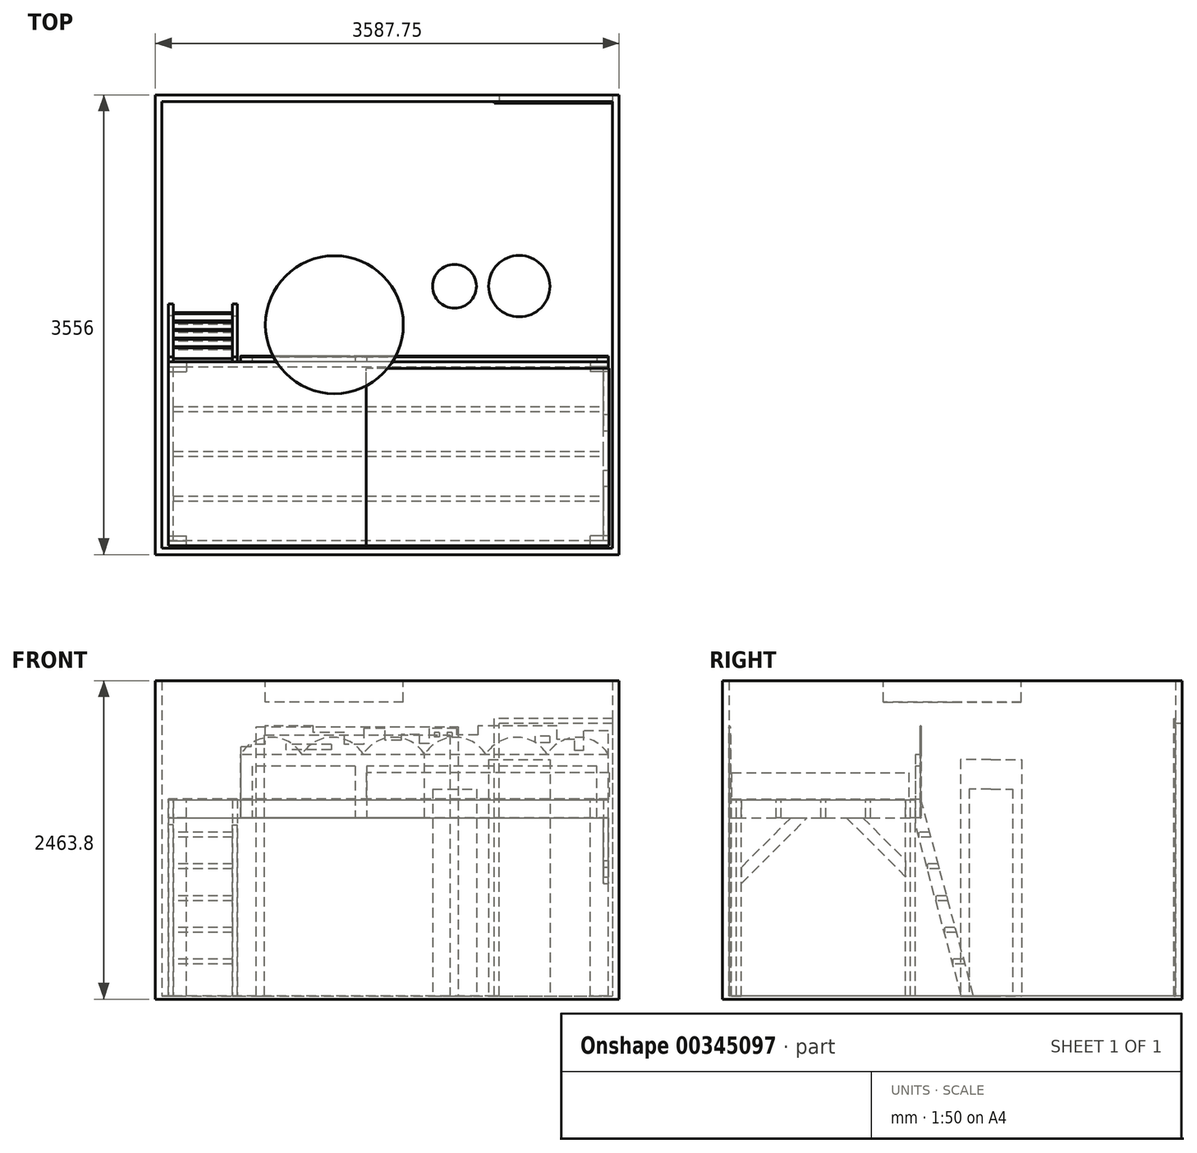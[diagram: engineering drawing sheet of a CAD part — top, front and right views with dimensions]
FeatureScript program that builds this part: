
annotation { "Feature Type Name" : "Feature", "Feature Type Description" : "" }
export const myFeature = defineFeature(function(context is Context, id is Id, definition is map)
    precondition{}
    {
        {
            var Q0;
            Q0=qCreatedBy(makeId("Top.planeOp"),FACE);
            var sketch = newSketch(context, id + "F0", { "sketchPlane" : qUnion([Q0])});
            skLineSegment(sketch, "E0.bottom", {"start": v(-2262.88, 2923.08) * mm, "end": v(-56.88, 2923.08) * mm});
            skLineSegment(sketch, "E0.top", {"start": v(-2262.88, -531.32) * mm, "end": v(1223.27, -531.32) * mm});
            skLineSegment(sketch, "E0.left", {"start": v(-2262.88, 2923.08) * mm, "end": v(-2262.88, -531.32) * mm});
            skLineSegment(sketch, "E0.right", {"start": v(1223.27, 2923.08) * mm, "end": v(1223.27, -531.32) * mm});
            skLineSegment(sketch, "E1.0", {"start": v(-2313.68, 2973.88) * mm, "end": v(-56.88, 2973.88) * mm});
            skLineSegment(sketch, "E1.1", {"start": v(-2313.68, 2973.88) * mm, "end": v(-2313.68, -582.12) * mm});
            skLineSegment(sketch, "E1.2", {"start": v(-2313.68, -582.12) * mm, "end": v(1274.07, -582.12) * mm});
            skLineSegment(sketch, "E1.3", {"start": v(1274.07, 2973.88) * mm, "end": v(1274.07, -582.12) * mm});
            skLineSegment(sketch, "E2.bottom", {"start": v(-94.98, 2923.08) * mm, "end": v(-56.88, 2923.08) * mm});
            skLineSegment(sketch, "E2.top", {"start": v(-94.98, 2910.38) * mm, "end": v(-56.88, 2910.38) * mm});
            skLineSegment(sketch, "E2.left", {"start": v(-94.98, 2923.08) * mm, "end": v(-94.98, 2910.38) * mm});
            skLineSegment(sketch, "E2.right", {"start": v(-56.88, 2923.08) * mm, "end": v(-56.88, 2910.38) * mm});
            skLineSegment(sketch, "E3", {"start": v(-56.88, 2923.08) * mm, "end": v(-56.88, 2973.88) * mm});
            skLineSegment(sketch, "E4", {"start": v(1274.07, 2973.88) * mm, "end": v(1223.27, 2973.88) * mm});
            skLineSegment(sketch, "E5", {"start": v(1223.27, 2973.88) * mm, "end": v(1223.27, 2923.08) * mm});
            skLineSegment(sketch, "E6", {"start": v(-56.88, 2973.88) * mm, "end": v(1223.27, 2973.88) * mm});
            skLineSegment(sketch, "E7", {"start": v(1223.27, 2923.08) * mm, "end": v(-56.88, 2923.08) * mm});
            skSolve(sketch);
        }
        {
            var Q0;
            Q0=qSketchRegion(id+"F0",true);
            extrude(context, id + "F1", {"entities" : qUnion([Q0]), "depth" : 2438.4 * mm});
        }
        {
            var Q0;
            Q0=makeQuery(id+"F1.opExtrude","SWEPT_FACE",FACE,{"disambiguationData":[OSD([sQuery(id+"F0.wireOp",EDGE,"E0.bottom"),sQuery(id+"F0.wireOp",EDGE,"E2.bottom"),sQuery(id+"F0.wireOp",EDGE,"E7")])]});
            var sketch = newSketch(context, id + "F2", { "sketchPlane" : qUnion([Q0])});
            skLineSegment(sketch, "E8.bottom", {"start": v(1223.27, 0) * mm, "end": v(346.97, 0) * mm});
            skLineSegment(sketch, "E8.top", {"start": v(1223.27, 2108.2) * mm, "end": v(346.97, 2108.2) * mm});
            skLineSegment(sketch, "E8.left", {"start": v(1223.27, 0) * mm, "end": v(1223.27, 2108.2) * mm});
            skLineSegment(sketch, "E8.right", {"start": v(346.97, 0) * mm, "end": v(346.97, 2108.2) * mm});
            skSolve(sketch);
        }
        {
            var Q0;
            Q0=qSketchRegion(id+"F2",true);
            extrude(context, id + "F3", {"entities" : qUnion([Q0]), "operationType" : NewBodyOperationType.REMOVE, "endBound" : BoundingType.UP_TO_NEXT, "oppositeDirection" : true, "depth" : 25.4 * mm});
        }
        {
            var Q0;
            Q0=makeQuery(id+"F1.opExtrude","SWEPT_FACE",FACE,{"disambiguationData":[OSD([sQuery(id+"F0.wireOp",EDGE,"E0.bottom"),sQuery(id+"F0.wireOp",EDGE,"E2.bottom"),sQuery(id+"F0.wireOp",EDGE,"E7")])]});
            var sketch = newSketch(context, id + "F4", { "sketchPlane" : qUnion([Q0])});
            skLineSegment(sketch, "E9.bottom", {"start": v(346.97, 0) * mm, "end": v(308.87, 0) * mm});
            skLineSegment(sketch, "E9.top", {"start": v(346.97, 2146.3) * mm, "end": v(308.87, 2146.3) * mm});
            skLineSegment(sketch, "E9.left", {"start": v(346.97, 0) * mm, "end": v(346.97, 2146.3) * mm});
            skLineSegment(sketch, "E9.right", {"start": v(308.87, 0) * mm, "end": v(308.87, 2146.3) * mm});
            skLineSegment(sketch, "E10.bottom", {"start": v(346.97, 2146.3) * mm, "end": v(1223.27, 2146.3) * mm});
            skLineSegment(sketch, "E10.top", {"start": v(346.97, 2108.2) * mm, "end": v(1223.27, 2108.2) * mm});
            skLineSegment(sketch, "E10.left", {"start": v(346.97, 2146.3) * mm, "end": v(346.97, 2108.2) * mm});
            skLineSegment(sketch, "E10.right", {"start": v(1223.27, 2146.3) * mm, "end": v(1223.27, 2108.2) * mm});
            skSolve(sketch);
        }
        {
            var Q0;
            Q0=qSketchRegion(id+"F4",true);
            extrude(context, id + "F5", {"entities" : qUnion([Q0]), "operationType" : NewBodyOperationType.ADD, "depth" : 12.7 * mm});
        }
        {
            var Q0;
            Q0=makeQuery(id+"F1.opExtrude","CAP_FACE",FACE,{"disambiguationData":[OSD([sQuery(id+"F0.wireOp",EDGE,"E0.bottom"),sQuery(id+"F0.wireOp",EDGE,"E0.top"),sQuery(id+"F0.wireOp",EDGE,"E0.left"),sQuery(id+"F0.wireOp",EDGE,"E0.right"),sQuery(id+"F0.wireOp",EDGE,"E1.0"),sQuery(id+"F0.wireOp",EDGE,"E1.1"),sQuery(id+"F0.wireOp",EDGE,"E1.2"),sQuery(id+"F0.wireOp",EDGE,"E1.3"),sQuery(id+"F0.wireOp",EDGE,"E2.bottom"),sQuery(id+"F0.wireOp",EDGE,"E4"),sQuery(id+"F0.wireOp",EDGE,"E6"),sQuery(id+"F0.wireOp",EDGE,"E7")])],"isStart":false});
            var sketch = newSketch(context, id + "F6", { "sketchPlane" : qUnion([Q0])});
            skCircle(sketch, "E11", {"center": v(-929.38, 1195.88) * mm, "radius": 533.4 * mm});
            skSolve(sketch);
        }
        {
            var Q0;
            Q0=qSketchRegion(id+"F6",true);
            extrude(context, id + "F7", {"entities" : qUnion([Q0]), "oppositeDirection" : true, "depth" : 165.1 * mm});
        }
        {
            var Q0;
            Q0=makeQuery(id+"F5.boolean.opBoolean","MERGE",FACE,{"derivedFrom":[makeQuery(id+"F1.opExtrude","CAP_FACE",FACE,{"disambiguationData":[OSD([sQuery(id+"F0.wireOp",EDGE,"E0.bottom"),sQuery(id+"F0.wireOp",EDGE,"E0.top"),sQuery(id+"F0.wireOp",EDGE,"E0.left"),sQuery(id+"F0.wireOp",EDGE,"E0.right"),sQuery(id+"F0.wireOp",EDGE,"E1.0"),sQuery(id+"F0.wireOp",EDGE,"E1.1"),sQuery(id+"F0.wireOp",EDGE,"E1.2"),sQuery(id+"F0.wireOp",EDGE,"E1.3"),sQuery(id+"F0.wireOp",EDGE,"E2.bottom"),sQuery(id+"F0.wireOp",EDGE,"E4"),sQuery(id+"F0.wireOp",EDGE,"E6"),sQuery(id+"F0.wireOp",EDGE,"E7")])],"isStart":true}),makeQuery(id+"F5.opExtrude","SWEPT_FACE",FACE,{"disambiguationData":[OSD([sQuery(id+"F4.wireOp",EDGE,"E9.bottom")])]})]});
            var sketch = newSketch(context, id + "F8", { "sketchPlane" : qUnion([Q0])});
            skLineSegment(sketch, "E12.bottom", {"start": v(-2313.68, -2973.88) * mm, "end": v(1274.07, -2973.88) * mm});
            skLineSegment(sketch, "E12.top", {"start": v(-2313.68, 582.12) * mm, "end": v(1274.07, 582.12) * mm});
            skLineSegment(sketch, "E12.left", {"start": v(-2313.68, -2973.88) * mm, "end": v(-2313.68, 582.12) * mm});
            skLineSegment(sketch, "E12.right", {"start": v(1274.07, -2973.88) * mm, "end": v(1274.07, 582.12) * mm});
            skSolve(sketch);
        }
        {
            var Q0;
            Q0=qSketchRegion(id+"F8",true);
            extrude(context, id + "F9", {"entities" : qUnion([Q0]), "operationType" : NewBodyOperationType.ADD, "depth" : 25.4 * mm});
        }
        {
            var Q0;
            Q0=makeQuery(id+"F9.opExtrude","CAP_FACE",FACE,{"disambiguationData":[OSD([sQuery(id+"F8.wireOp",EDGE,"E12.bottom"),sQuery(id+"F8.wireOp",EDGE,"E12.top"),sQuery(id+"F8.wireOp",EDGE,"E12.left"),sQuery(id+"F8.wireOp",EDGE,"E12.right")])],"isStart":true});
            cPlane(context, id + "F10", {"entities" : qUnion([Q0]), "cplaneType" : CPlaneType.OFFSET, "offset" : 1524 * mm, "width" : 152.4 * mm, "height" : 152.4 * mm});
        }
        {
            var Q0;
            Q0=makeQuery(id+"F1.opExtrude","SWEPT_FACE",FACE,{"disambiguationData":[OSD([sQuery(id+"F0.wireOp",EDGE,"E0.top")])]});
            var sketch = newSketch(context, id + "F11", { "sketchPlane" : qUnion([Q0])});
            skLineSegment(sketch, "E13.bottom", {"start": v(1532.63, 0) * mm, "end": v(1469.13, 0) * mm});
            skLineSegment(sketch, "E13.top", {"start": v(1532.63, 2082.8) * mm, "end": v(1469.13, 2082.8) * mm});
            skLineSegment(sketch, "E13.left", {"start": v(1532.63, 0) * mm, "end": v(1532.63, 2082.8) * mm});
            skLineSegment(sketch, "E13.right", {"start": v(1469.13, 0) * mm, "end": v(1469.13, 2082.8) * mm});
            skLineSegment(sketch, "E14.bottom", {"start": v(1469.13, 2082.8) * mm, "end": v(34.03, 2082.8) * mm});
            skLineSegment(sketch, "E14.top", {"start": v(1469.13, 2019.3) * mm, "end": v(34.03, 2019.3) * mm});
            skLineSegment(sketch, "E14.left", {"start": v(1469.13, 2082.8) * mm, "end": v(1469.13, 2019.3) * mm});
            skLineSegment(sketch, "E14.right", {"start": v(34.03, 2082.8) * mm, "end": v(34.03, 2019.3) * mm});
            skLineSegment(sketch, "E15.bottom", {"start": v(34.03, 2082.8) * mm, "end": v(-29.47, 2082.8) * mm});
            skLineSegment(sketch, "E15.top", {"start": v(34.03, 0) * mm, "end": v(-29.47, 0) * mm});
            skLineSegment(sketch, "E15.left", {"start": v(34.03, 2082.8) * mm, "end": v(34.03, 0) * mm});
            skLineSegment(sketch, "E15.right", {"start": v(-29.47, 2082.8) * mm, "end": v(-29.47, 0) * mm});
            skSolve(sketch);
        }
        {
            var Q0;
            Q0=qSketchRegion(id+"F11",true);
            extrude(context, id + "F12", {"entities" : qUnion([Q0]), "operationType" : NewBodyOperationType.ADD, "depth" : 12.7 * mm});
        }
        {
            var Q0;
            Q0=qCreatedBy(id+"F10.planeOp",FACE);
            var sketch = newSketch(context, id + "F13", { "sketchPlane" : qUnion([Q0])});
            skLineSegment(sketch, "E16.bottom", {"start": v(1197.87, -512.27) * mm, "end": v(-681.73, -512.27) * mm});
            skLineSegment(sketch, "E16.top", {"start": v(1197.87, 859.33) * mm, "end": v(-681.73, 859.33) * mm});
            skLineSegment(sketch, "E16.left", {"start": v(1197.87, -512.27) * mm, "end": v(1197.87, 859.33) * mm});
            skLineSegment(sketch, "E16.right", {"start": v(-681.73, -512.27) * mm, "end": v(-681.73, 859.33) * mm});
            skSolve(sketch);
        }
        {
            var Q0;
            Q0=qSketchRegion(id+"F13",true);
            extrude(context, id + "F14", {"entities" : qUnion([Q0]), "depth" : 203.2 * mm});
        }
        {
            var Q0;
            Q0=qCreatedBy(id+"F10.planeOp",FACE);
            var sketch = newSketch(context, id + "F15", { "sketchPlane" : qUnion([Q0])});
            skLineSegment(sketch, "E17.bottom", {"start": v(1191.52, -512.27) * mm, "end": v(-2212.08, -512.27) * mm});
            skLineSegment(sketch, "E17.top", {"start": v(1191.52, 910.13) * mm, "end": v(-2212.08, 910.13) * mm});
            skLineSegment(sketch, "E17.left", {"start": v(1191.52, -512.27) * mm, "end": v(1191.52, 910.13) * mm});
            skLineSegment(sketch, "E17.right", {"start": v(-2212.08, -512.27) * mm, "end": v(-2212.08, 910.13) * mm});
            skSolve(sketch);
        }
        {
            var Q0;
            Q0=qSketchRegion(id+"F15",true);
            extrude(context, id + "F16", {"entities" : qUnion([Q0]), "oppositeDirection" : true, "depth" : 6.35 * mm});
        }
        {
            var Q0;
            Q0=makeQuery(id+"F16.opExtrude","CAP_FACE",FACE,{"disambiguationData":[OSD([sQuery(id+"F15.wireOp",EDGE,"E17.bottom"),sQuery(id+"F15.wireOp",EDGE,"E17.top"),sQuery(id+"F15.wireOp",EDGE,"E17.left"),sQuery(id+"F15.wireOp",EDGE,"E17.right")])],"isStart":false});
            var sketch = newSketch(context, id + "F17", { "sketchPlane" : qUnion([Q0])});
            skLineSegment(sketch, "E18.bottom", {"start": v(-2212.08, 474.17) * mm, "end": v(-2173.98, 474.17) * mm});
            skLineSegment(sketch, "E18.top", {"start": v(-2212.08, -872.03) * mm, "end": v(-2173.98, -872.03) * mm});
            skLineSegment(sketch, "E18.left", {"start": v(-2212.08, 474.17) * mm, "end": v(-2212.08, -872.03) * mm});
            skLineSegment(sketch, "E18.right", {"start": v(-2173.98, 474.17) * mm, "end": v(-2173.98, -872.03) * mm});
            skLineSegment(sketch, "E19.bottom", {"start": v(1191.52, 474.17) * mm, "end": v(1153.42, 474.17) * mm});
            skLineSegment(sketch, "E19.top", {"start": v(1191.52, -872.03) * mm, "end": v(1153.42, -872.03) * mm});
            skLineSegment(sketch, "E19.left", {"start": v(1191.52, 474.17) * mm, "end": v(1191.52, -872.03) * mm});
            skLineSegment(sketch, "E19.right", {"start": v(1153.42, 474.17) * mm, "end": v(1153.42, -872.03) * mm});
            skLineSegment(sketch, "E20.0", {"start": v(-2212.08, 512.27) * mm, "end": v(-2212.08, -910.13) * mm, "construction": true});
            skLineSegment(sketch, "E21.0", {"start": v(1191.52, 512.27) * mm, "end": v(1191.52, -910.13) * mm, "construction": true});
            skSolve(sketch);
        }
        {
            var Q0;
            Q0=qSketchRegion(id+"F17",true);
            extrude(context, id + "F18", {"entities" : qUnion([Q0]), "depth" : 139.7 * mm});
        }
        {
            var Q0;
            Q0=makeQuery(id+"F16.opExtrude","CAP_FACE",FACE,{"disambiguationData":[OSD([sQuery(id+"F15.wireOp",EDGE,"E17.bottom"),sQuery(id+"F15.wireOp",EDGE,"E17.top"),sQuery(id+"F15.wireOp",EDGE,"E17.left"),sQuery(id+"F15.wireOp",EDGE,"E17.right")])],"isStart":false});
            var sketch = newSketch(context, id + "F19", { "sketchPlane" : qUnion([Q0])});
            skPoint(sketch, "E22.0", {"position": v(-2173.98, 474.17) * mm});
            skPoint(sketch, "E23.0", {"position": v(1153.42, 474.17) * mm});
            skPoint(sketch, "E24.0", {"position": v(1191.52, -910.13) * mm});
            skPoint(sketch, "E25.0", {"position": v(-2212.08, -910.13) * mm});
            skLineSegment(sketch, "E26.0", {"start": v(1191.52, 512.27) * mm, "end": v(-2212.08, 512.27) * mm, "construction": true});
            skLineSegment(sketch, "E27.top", {"start": v(-2212.08, -872.03) * mm, "end": v(1191.52, -872.03) * mm});
            skLineSegment(sketch, "E27.right", {"start": v(1191.52, -910.13) * mm, "end": v(1191.52, -872.03) * mm});
            skLineSegment(sketch, "E28", {"start": v(1191.52, -910.13) * mm, "end": v(-2212.08, -910.13) * mm});
            skLineSegment(sketch, "E29", {"start": v(-2212.08, -910.13) * mm, "end": v(-2212.08, -872.03) * mm});
            skLineSegment(sketch, "E30", {"start": v(1191.52, -872.03) * mm, "end": v(1191.52, -910.13) * mm});
            skLineSegment(sketch, "E31.0.1.0", {"start": v(-2212.08, 512.27) * mm, "end": v(1191.52, 512.27) * mm});
            skLineSegment(sketch, "E31.0.1.1", {"start": v(1191.52, 474.17) * mm, "end": v(-2212.08, 474.17) * mm});
            skLineSegment(sketch, "E31.0.1.2", {"start": v(1191.52, 512.27) * mm, "end": v(1191.52, 474.17) * mm});
            skLineSegment(sketch, "E31.0.1.3", {"start": v(-2212.08, 474.17) * mm, "end": v(-2212.08, 512.27) * mm});
            skLineSegment(sketch, "E31.direction1", {"start": v(-2212.08, -872.03) * mm, "end": v(-2165.04, -872.03) * mm, "construction": true});
            skLineSegment(sketch, "E31.direction2", {"start": v(-2212.08, -872.03) * mm, "end": v(-2212.08, 512.27) * mm, "construction": true});
            skPoint(sketch, "E32.0", {"position": v(-2212.08, -872.03) * mm});
            skPoint(sketch, "E33.0", {"position": v(1191.52, -872.03) * mm});
            skPoint(sketch, "E34.startSnap0", {"position": v(-510.28, 512.27) * mm});
            skLineSegment(sketch, "E35.0", {"start": v(-2173.98, 474.17) * mm, "end": v(-2173.98, -872.03) * mm, "construction": true});
            skLineSegment(sketch, "E36.0", {"start": v(1153.42, 474.17) * mm, "end": v(1153.42, -872.03) * mm, "construction": true});
            skLineSegment(sketch, "E37.bottom", {"start": v(-2173.98, -179.88) * mm, "end": v(1153.42, -179.88) * mm});
            skLineSegment(sketch, "E37.top", {"start": v(-2173.98, -217.98) * mm, "end": v(1153.42, -217.98) * mm});
            skLineSegment(sketch, "E37.left", {"start": v(-2173.98, -179.88) * mm, "end": v(-2173.98, -217.98) * mm});
            skLineSegment(sketch, "E37.right", {"start": v(1153.42, -179.88) * mm, "end": v(1153.42, -217.98) * mm});
            skPoint(sketch, "E38", {"position": v(-2173.98, -198.93) * mm});
            skPoint(sketch, "E39", {"position": v(1153.42, -198.93) * mm});
            skLineSegment(sketch, "E40", {"start": v(-510.28, -179.88) * mm, "end": v(-510.28, 474.17) * mm, "construction": true});
            skLineSegment(sketch, "E41", {"start": v(-510.28, -872.03) * mm, "end": v(-510.28, -217.98) * mm, "construction": true});
            skPoint(sketch, "E42", {"position": v(-510.28, 147.15) * mm});
            skLineSegment(sketch, "E43.left", {"start": v(1153.42, 0) * mm, "end": v(1153.42, 197.18) * mm});
            skLineSegment(sketch, "E43.right", {"start": v(-2173.98, 97.12) * mm, "end": v(-2173.98, 294.3) * mm});
            skLineSegment(sketch, "E44.bottom", {"start": v(-2173.98, 128.1) * mm, "end": v(1153.42, 128.1) * mm});
            skLineSegment(sketch, "E44.top", {"start": v(-2173.98, 166.2) * mm, "end": v(1153.42, 166.2) * mm});
            skLineSegment(sketch, "E44.left", {"start": v(-2173.98, 128.1) * mm, "end": v(-2173.98, 166.2) * mm});
            skLineSegment(sketch, "E44.right", {"start": v(1153.42, 128.1) * mm, "end": v(1153.42, 166.2) * mm});
            skLineSegment(sketch, "E45", {"start": v(-2173.98, -198.93) * mm, "end": v(1153.42, -198.93) * mm, "construction": true});
            skLineSegment(sketch, "E46.MirrorCS", {"start": v(-2173.98, -525.95) * mm, "end": v(1153.42, -525.95) * mm});
            skLineSegment(sketch, "E47.MirrorCS", {"start": v(-2173.98, -564.05) * mm, "end": v(1153.42, -564.05) * mm});
            skLineSegment(sketch, "E48", {"start": v(-2173.98, -525.95) * mm, "end": v(-2173.98, -564.05) * mm, "construction": true});
            skLineSegment(sketch, "E49", {"start": v(-2173.98, -525.95) * mm, "end": v(-2173.98, -564.05) * mm});
            skLineSegment(sketch, "E50", {"start": v(1153.42, -525.95) * mm, "end": v(1153.42, -564.05) * mm});
            skSolve(sketch);
        }
        {
            var Q0;
            Q0=qSketchRegion(id+"F19",true);
            extrude(context, id + "F20", {"entities" : qUnion([Q0]), "depth" : 139.7 * mm});
        }
        {
            var Q0;
            Q0=makeQuery(id+"F18.opExtrude","SWEPT_FACE",FACE,{"disambiguationData":[OSD([sQuery(id+"F17.wireOp",EDGE,"E18.left")])]});
            var sketch = newSketch(context, id + "F21", { "sketchPlane" : qUnion([Q0])});
            skPoint(sketch, "E51.0", {"position": v(-910.13, 1524) * mm});
            skPoint(sketch, "E52.0", {"position": v(-910.13, 1377.95) * mm});
            skLineSegment(sketch, "E53", {"start": v(-910.13, 1524) * mm, "end": v(-948.23, 1524) * mm});
            skLineSegment(sketch, "E54", {"start": v(-948.23, 1524) * mm, "end": v(-1356.58, 0) * mm});
            skLineSegment(sketch, "E55", {"start": v(-1356.58, 0) * mm, "end": v(-1264.54, 0) * mm});
            skLineSegment(sketch, "E56", {"start": v(-1264.54, 0) * mm, "end": v(-910.13, 1322.7) * mm});
            skLineSegment(sketch, "E57", {"start": v(-910.13, 1524) * mm, "end": v(-910.13, 1322.7) * mm});
            skLineSegment(sketch, "E58.0", {"start": v(-2973.88, -25.4) * mm, "end": v(582.12, -25.4) * mm, "construction": true});
            skLineSegment(sketch, "E59.0.0", {"start": v(531.32, 0) * mm, "end": v(518.62, 0) * mm, "construction": true});
            skLineSegment(sketch, "E59.0.2", {"start": v(518.62, 0) * mm, "end": v(531.32, 0) * mm, "construction": true});
            skLineSegment(sketch, "E59.0.4", {"start": v(531.32, 0) * mm, "end": v(-2973.88, 0) * mm, "construction": true});
            skLineSegment(sketch, "E59.0.6", {"start": v(-2973.88, 0) * mm, "end": v(-2910.38, 0) * mm, "construction": true});
            skLineSegment(sketch, "E59.0.8", {"start": v(-2910.38, 0) * mm, "end": v(-2923.08, 0) * mm, "construction": true});
            skLineSegment(sketch, "E59.0.10", {"start": v(-2923.08, 0) * mm, "end": v(531.32, 0) * mm, "construction": true});
            skLineSegment(sketch, "E59.0.12", {"start": v(531.32, 0) * mm, "end": v(518.62, 0) * mm, "construction": true});
            skLineSegment(sketch, "E59.0.14", {"start": v(518.62, 0) * mm, "end": v(531.32, 0) * mm, "construction": true});
            skSolve(sketch);
        }
        {
            var Q0;
            Q0=qSketchRegion(id+"F21",true);
            extrude(context, id + "F22", {"entities" : qUnion([Q0]), "oppositeDirection" : true, "depth" : 38.1 * mm});
        }
        {
            var Q0;
            Q0=makeQuery(id+"F22.opExtrude","CAP_FACE",FACE,{"disambiguationData":[OSD([sQuery(id+"F21.wireOp",EDGE,"E53"),sQuery(id+"F21.wireOp",EDGE,"E54"),sQuery(id+"F21.wireOp",EDGE,"E55"),sQuery(id+"F21.wireOp",EDGE,"E56"),sQuery(id+"F21.wireOp",EDGE,"E57")])],"isStart":false});
            var sketch = newSketch(context, id + "F23", { "sketchPlane" : qUnion([Q0])});
            skLineSegment(sketch, "E60.bottom", {"start": v(1280.42, 284.22) * mm, "end": v(1198.6, 284.22) * mm});
            skLineSegment(sketch, "E60.top", {"start": v(1290.63, 246.12) * mm, "end": v(1198.6, 246.12) * mm});
            skLineSegment(sketch, "E60.left", {"start": v(1280.42, 284.22) * mm, "end": v(1290.63, 246.12) * mm});
            skLineSegment(sketch, "E60.right", {"start": v(1198.6, 284.22) * mm, "end": v(1198.6, 246.12) * mm});
            skLineSegment(sketch, "E61.0.1.0", {"start": v(1214.68, 529.57) * mm, "end": v(1132.86, 529.57) * mm});
            skLineSegment(sketch, "E61.0.1.1", {"start": v(1224.9, 491.47) * mm, "end": v(1132.86, 491.47) * mm});
            skLineSegment(sketch, "E61.0.1.2", {"start": v(1214.68, 529.57) * mm, "end": v(1224.9, 491.47) * mm});
            skLineSegment(sketch, "E61.0.1.3", {"start": v(1132.86, 529.57) * mm, "end": v(1132.86, 491.47) * mm});
            skLineSegment(sketch, "E61.0.2.0", {"start": v(1148.94, 774.92) * mm, "end": v(1067.12, 774.92) * mm});
            skLineSegment(sketch, "E61.0.2.1", {"start": v(1159.15, 736.82) * mm, "end": v(1067.12, 736.82) * mm});
            skLineSegment(sketch, "E61.0.2.2", {"start": v(1148.94, 774.92) * mm, "end": v(1159.15, 736.82) * mm});
            skLineSegment(sketch, "E61.0.2.3", {"start": v(1067.12, 774.92) * mm, "end": v(1067.12, 736.82) * mm});
            skLineSegment(sketch, "E61.0.3.0", {"start": v(1083.2, 1020.26) * mm, "end": v(1001.38, 1020.26) * mm});
            skLineSegment(sketch, "E61.0.3.1", {"start": v(1093.41, 982.16) * mm, "end": v(1001.38, 982.16) * mm});
            skLineSegment(sketch, "E61.0.3.2", {"start": v(1083.2, 1020.26) * mm, "end": v(1093.41, 982.16) * mm});
            skLineSegment(sketch, "E61.0.3.3", {"start": v(1001.38, 1020.26) * mm, "end": v(1001.38, 982.16) * mm});
            skLineSegment(sketch, "E61.0.4.0", {"start": v(1017.46, 1265.6) * mm, "end": v(935.64, 1265.6) * mm});
            skLineSegment(sketch, "E61.0.4.1", {"start": v(1027.67, 1227.5) * mm, "end": v(935.64, 1227.5) * mm});
            skLineSegment(sketch, "E61.0.4.2", {"start": v(1017.46, 1265.6) * mm, "end": v(1027.67, 1227.5) * mm});
            skLineSegment(sketch, "E61.0.4.3", {"start": v(935.64, 1265.6) * mm, "end": v(935.64, 1227.5) * mm});
            skLineSegment(sketch, "E61.direction1", {"start": v(1198.6, 246.12) * mm, "end": v(1243.47, 246.12) * mm, "construction": true});
            skLineSegment(sketch, "E61.direction2", {"start": v(1198.6, 246.12) * mm, "end": v(1132.86, 491.47) * mm, "construction": true});
            skLineSegment(sketch, "E62.0", {"start": v(948.23, 1524) * mm, "end": v(1356.58, 0) * mm, "construction": true});
            skSolve(sketch);
        }
        {
            var Q0;
            Q0=qSketchRegion(id+"F23",true);
            extrude(context, id + "F24", {"entities" : qUnion([Q0]), "depth" : 457.2 * mm});
        }
        {
            var Q0;
            Q0=makeQuery(id+"F22.opExtrude","CAP_FACE",FACE,{"disambiguationData":[OSD([sQuery(id+"F21.wireOp",EDGE,"E53"),sQuery(id+"F21.wireOp",EDGE,"E54"),sQuery(id+"F21.wireOp",EDGE,"E55"),sQuery(id+"F21.wireOp",EDGE,"E56"),sQuery(id+"F21.wireOp",EDGE,"E57")])],"isStart":true});
            cPlane(context, id + "F25", {"entities" : qUnion([Q0]), "cplaneType" : CPlaneType.OFFSET, "offset" : 266.7 * mm, "oppositeDirection" : true, "width" : 152.4 * mm, "height" : 152.4 * mm});
        }
        {
            var Q0;
            Q0=makeQuery(id+"F22.opExtrude","SWEPT_BODY",BODY,{"disambiguationData":[OSD([sQuery(id+"F21.wireOp",EDGE,"E53"),sQuery(id+"F21.wireOp",EDGE,"E54"),sQuery(id+"F21.wireOp",EDGE,"E55"),sQuery(id+"F21.wireOp",EDGE,"E56"),sQuery(id+"F21.wireOp",EDGE,"E57")])]});
            var Q1;
            Q1=qCreatedBy(id+"F25.planeOp",FACE);
            mirror(context, id + "F26", {"entities" : qUnion([Q0]), "mirrorPlane" : qUnion([Q1])});
        }
        {
            var Q0;
            Q0=makeQuery(id+"F20.opExtrude","SWEPT_FACE",FACE,{"disambiguationData":[OSD([sQuery(id+"F19.wireOp",EDGE,"E28")])]});
            var sketch = newSketch(context, id + "F27", { "sketchPlane" : qUnion([Q0])});
            skLineSegment(sketch, "E63.0", {"start": v(-1191.52, 1377.95) * mm, "end": v(-1191.52, 1517.65) * mm, "construction": true});
            skLineSegment(sketch, "E64.0", {"start": v(-1191.52, 1377.95) * mm, "end": v(2212.08, 1377.95) * mm, "construction": true});
            skPoint(sketch, "E65.0", {"position": v(-1172.47, 1377.95) * mm});
            skLineSegment(sketch, "E66.bottom", {"start": v(-1191.52, 1377.95) * mm, "end": v(-1102.62, 1377.95) * mm});
            skLineSegment(sketch, "E66.top", {"start": v(-1191.52, 1866.9) * mm, "end": v(-1102.62, 1866.9) * mm});
            skLineSegment(sketch, "E66.left", {"start": v(-1191.52, 1377.95) * mm, "end": v(-1191.52, 1866.9) * mm});
            skLineSegment(sketch, "E66.right", {"start": v(-1102.62, 1377.95) * mm, "end": v(-1102.62, 1866.9) * mm});
            skLineSegment(sketch, "E67.bottom", {"start": v(-1102.62, 1866.9) * mm, "end": v(1653.28, 1866.9) * mm});
            skLineSegment(sketch, "E67.top", {"start": v(-1102.62, 1778) * mm, "end": v(1653.28, 1778) * mm});
            skLineSegment(sketch, "E67.left", {"start": v(-1102.62, 1866.9) * mm, "end": v(-1102.62, 1778) * mm});
            skLineSegment(sketch, "E67.right", {"start": v(1653.28, 1866.9) * mm, "end": v(1653.28, 1778) * mm});
            skLineSegment(sketch, "E68.bottom", {"start": v(1653.28, 1778) * mm, "end": v(1564.38, 1778) * mm});
            skLineSegment(sketch, "E68.top", {"start": v(1653.28, 1377.95) * mm, "end": v(1564.38, 1377.95) * mm});
            skLineSegment(sketch, "E68.left", {"start": v(1653.28, 1778) * mm, "end": v(1653.28, 1377.95) * mm});
            skLineSegment(sketch, "E68.right", {"start": v(1564.38, 1778) * mm, "end": v(1564.38, 1377.95) * mm});
            skLineSegment(sketch, "E69.bottom", {"start": v(679.14, 1778) * mm, "end": v(768.04, 1778) * mm});
            skLineSegment(sketch, "E69.top", {"start": v(679.14, 1377.95) * mm, "end": v(768.04, 1377.95) * mm});
            skLineSegment(sketch, "E69.left", {"start": v(679.14, 1778) * mm, "end": v(679.14, 1377.95) * mm});
            skLineSegment(sketch, "E69.right", {"start": v(768.04, 1778) * mm, "end": v(768.04, 1377.95) * mm});
            skLineSegment(sketch, "E70.0", {"start": v(1678.68, 1524) * mm, "end": v(1678.68, 1322.7) * mm, "construction": true});
            skSolve(sketch);
        }
        {
            var Q0;
            Q0=qSketchRegion(id+"F27",true);
            extrude(context, id + "F28", {"entities" : qUnion([Q0]), "depth" : 38.1 * mm});
        }
        {
            var Q0;
            Q0=makeQuery(id+"F28.opExtrude","CAP_FACE",FACE,{"disambiguationData":[OSD([sQuery(id+"F27.wireOp",EDGE,"E66.bottom"),sQuery(id+"F27.wireOp",EDGE,"E66.top"),sQuery(id+"F27.wireOp",EDGE,"E66.left"),sQuery(id+"F27.wireOp",EDGE,"E66.right"),sQuery(id+"F27.wireOp",EDGE,"E67.bottom"),sQuery(id+"F27.wireOp",EDGE,"E67.top"),sQuery(id+"F27.wireOp",EDGE,"E67.right"),sQuery(id+"F27.wireOp",EDGE,"E68.top"),sQuery(id+"F27.wireOp",EDGE,"E68.left"),sQuery(id+"F27.wireOp",EDGE,"E68.right"),sQuery(id+"F27.wireOp",EDGE,"E69.top"),sQuery(id+"F27.wireOp",EDGE,"E69.left"),sQuery(id+"F27.wireOp",EDGE,"E69.right")])],"isStart":false});
            var sketch = newSketch(context, id + "F29", { "sketchPlane" : qUnion([Q0])});
            skArc(sketch, "E71", {"start": v(-402.96, 1866.9) * mm, "mid": v(-797.24, 2054.57) * mm, "end": v(-1191.52, 1866.9) * mm});
            skArc(sketch, "E72", {"start": v(-402.96, 1866.9) * mm, "mid": v(-8.69, 1679.23) * mm, "end": v(385.59, 1866.9) * mm});
            skArc(sketch, "E73", {"start": v(1174.14, 1866.9) * mm, "mid": v(779.87, 2054.57) * mm, "end": v(385.59, 1866.9) * mm});
            skLineSegment(sketch, "E74", {"start": v(-797.24, 1546.57) * mm, "end": v(779.87, 1546.57) * mm, "construction": true});
            skLineSegment(sketch, "E75", {"start": v(-1823.48, 2187.23) * mm, "end": v(1106.15, 2187.23) * mm, "construction": true});
            skLineSegment(sketch, "E76", {"start": v(-402.96, 1866.9) * mm, "end": v(-1191.52, 1866.9) * mm, "construction": true});
            skLineSegment(sketch, "E77", {"start": v(-402.96, 1866.9) * mm, "end": v(1174.14, 1866.9) * mm, "construction": true});
            skSolve(sketch);
        }
        {
            var Q0;
            {var subQ0=sQuery(id+"F29.wireOp",EDGE,"E72");var subQ3=sQuery(id+"F27.wireOp",EDGE,"E67.top");var subQ4=makeQuery(id+"F28.opExtrude","CAP_EDGE",EDGE,{"disambiguationData":[OSD([subQ3]),TDD([makeQuery(id+"F27.imprint","IMPRINT",EDGE,{"disambiguationData":[TD([[makeQuery(id+"F27.imprint","INTERSECT",VERTEX,{"derivedFrom":[sQuery(id+"F27.wireOp",EDGE,"E66.right"),subQ3,sQuery(id+"F27.wireOp",EDGE,"E67.left")]}),-1.0]])],"derivedFrom":subQ3})])],"isStart":false});var subQ5=makeQuery(id+"F29.imprint","INTERSECT",VERTEX,{"disambiguationData":[OD(0.0)],"derivedFrom":[subQ4,subQ0]});Q0=makeQuery(id+"F29.imprint","IMPRINT",FACE,{"disambiguationData":[TD([[makeQuery(id+"F29.imprint","IMPRINT",EDGE,{"disambiguationData":[TD([[subQ5,1.0]])],"derivedFrom":subQ0}),1.0]])]});}
            var sketch = newSketch(context, id + "F30", { "sketchPlane" : qUnion([Q0])});
            skLineSegment(sketch, "E78.0", {"start": v(-1191.52, 1377.95) * mm, "end": v(2212.08, 1377.95) * mm, "construction": true});
            skLineSegment(sketch, "E79.0", {"start": v(-1191.52, 1377.95) * mm, "end": v(-1191.52, 1866.9) * mm, "construction": true});
            skLineSegment(sketch, "E80.0", {"start": v(1653.28, 1866.9) * mm, "end": v(1653.28, 1377.95) * mm, "construction": true});
            skLineSegment(sketch, "E81.bottom", {"start": v(-1191.52, 1377.95) * mm, "end": v(1653.28, 1377.95) * mm});
            skLineSegment(sketch, "E81.top", {"start": v(-1191.52, 1866.9) * mm, "end": v(1653.28, 1866.9) * mm});
            skLineSegment(sketch, "E81.left", {"start": v(-1191.52, 1377.95) * mm, "end": v(-1191.52, 1866.9) * mm});
            skLineSegment(sketch, "E81.right", {"start": v(1653.28, 1377.95) * mm, "end": v(1653.28, 1866.9) * mm});
            skLineSegment(sketch, "E82.bottom", {"start": v(-1191.52, 1866.9) * mm, "end": v(-625.52, 1866.9) * mm});
            skLineSegment(sketch, "E82.top", {"start": v(-1191.52, 2023.58) * mm, "end": v(-625.52, 2023.58) * mm});
            skLineSegment(sketch, "E82.left", {"start": v(-1191.52, 1866.9) * mm, "end": v(-1191.52, 2023.58) * mm});
            skLineSegment(sketch, "E82.right", {"start": v(-625.52, 1866.9) * mm, "end": v(-625.52, 2023.58) * mm});
            skPoint(sketch, "E83.oppositeSnap0", {"position": v(-625.52, 1945.24) * mm});
            skLineSegment(sketch, "E83.bottom", {"start": v(-555.78, 1866.9) * mm, "end": v(-379.76, 1866.9) * mm});
            skLineSegment(sketch, "E83.top", {"start": v(-555.78, 1945.24) * mm, "end": v(-379.76, 1945.24) * mm});
            skLineSegment(sketch, "E83.left", {"start": v(-555.78, 1866.9) * mm, "end": v(-555.78, 1945.24) * mm});
            skLineSegment(sketch, "E83.right", {"start": v(-379.76, 1866.9) * mm, "end": v(-379.76, 1945.24) * mm});
            skLineSegment(sketch, "E84.bottom", {"start": v(-429.58, 1945.24) * mm, "end": v(-220.34, 1945.24) * mm});
            skLineSegment(sketch, "E84.top", {"start": v(-429.58, 2103.3) * mm, "end": v(-220.34, 2103.3) * mm});
            skLineSegment(sketch, "E84.left", {"start": v(-429.58, 1945.24) * mm, "end": v(-429.58, 2103.3) * mm});
            skLineSegment(sketch, "E84.right", {"start": v(-220.34, 1945.24) * mm, "end": v(-220.34, 2103.3) * mm});
            skLineSegment(sketch, "E85.bottom", {"start": v(-379.76, 1945.24) * mm, "end": v(-27.71, 1945.24) * mm});
            skLineSegment(sketch, "E85.top", {"start": v(-379.76, 1866.9) * mm, "end": v(-27.71, 1866.9) * mm});
            skLineSegment(sketch, "E85.left", {"start": v(-379.76, 1945.24) * mm, "end": v(-379.76, 1866.9) * mm});
            skLineSegment(sketch, "E85.right", {"start": v(-27.71, 1945.24) * mm, "end": v(-27.71, 1866.9) * mm});
            skLineSegment(sketch, "E86.bottom", {"start": v(0, 1945.24) * mm, "end": v(164.91, 1945.24) * mm});
            skLineSegment(sketch, "E86.top", {"start": v(0, 2062.85) * mm, "end": v(164.91, 2062.85) * mm});
            skLineSegment(sketch, "E86.left", {"start": v(0, 1945.24) * mm, "end": v(0, 2062.85) * mm});
            skLineSegment(sketch, "E86.right", {"start": v(164.91, 1945.24) * mm, "end": v(164.91, 2062.85) * mm});
            skLineSegment(sketch, "E87.bottom", {"start": v(223.92, 1866.9) * mm, "end": v(344.26, 1866.9) * mm});
            skLineSegment(sketch, "E87.top", {"start": v(223.92, 2063.44) * mm, "end": v(344.26, 2063.44) * mm});
            skLineSegment(sketch, "E87.left", {"start": v(223.92, 1866.9) * mm, "end": v(223.92, 2063.44) * mm});
            skLineSegment(sketch, "E87.right", {"start": v(344.26, 1866.9) * mm, "end": v(344.26, 2063.44) * mm});
            skLineSegment(sketch, "E88.bottom", {"start": v(344.26, 1965.17) * mm, "end": v(573.42, 1965.17) * mm});
            skLineSegment(sketch, "E88.top", {"start": v(344.26, 1866.9) * mm, "end": v(573.42, 1866.9) * mm});
            skLineSegment(sketch, "E88.left", {"start": v(344.26, 1965.17) * mm, "end": v(344.26, 1866.9) * mm});
            skLineSegment(sketch, "E88.right", {"start": v(573.42, 1965.17) * mm, "end": v(573.42, 1866.9) * mm});
            skLineSegment(sketch, "E89.bottom", {"start": v(493.71, 1965.17) * mm, "end": v(663.09, 1965.17) * mm});
            skLineSegment(sketch, "E89.top", {"start": v(493.71, 2083.36) * mm, "end": v(663.09, 2083.36) * mm});
            skLineSegment(sketch, "E89.left", {"start": v(493.71, 1965.17) * mm, "end": v(493.71, 2083.36) * mm});
            skLineSegment(sketch, "E89.right", {"start": v(663.09, 1965.17) * mm, "end": v(663.09, 2083.36) * mm});
            skLineSegment(sketch, "E90.bottom", {"start": v(573.42, 1965.17) * mm, "end": v(942.07, 1965.17) * mm});
            skLineSegment(sketch, "E90.top", {"start": v(573.42, 1866.9) * mm, "end": v(942.07, 1866.9) * mm});
            skLineSegment(sketch, "E91.top", {"start": v(862.36, 1866.9) * mm, "end": v(1181.2, 1866.9) * mm});
            skLineSegment(sketch, "E92.bottom", {"start": v(812.54, 2060.12) * mm, "end": v(1061.63, 2060.12) * mm});
            skLineSegment(sketch, "E92.top", {"start": v(812.54, 1866.9) * mm, "end": v(1061.63, 1866.9) * mm});
            skLineSegment(sketch, "E92.left", {"start": v(812.54, 2060.12) * mm, "end": v(812.54, 1866.9) * mm});
            skLineSegment(sketch, "E92.right", {"start": v(1061.63, 2060.12) * mm, "end": v(1061.63, 1866.9) * mm});
            skLineSegment(sketch, "E93.bottom", {"start": v(1061.63, 1993.7) * mm, "end": v(1181.2, 1993.7) * mm});
            skLineSegment(sketch, "E94.bottom", {"start": v(1373.82, 1866.9) * mm, "end": v(1141.34, 1866.9) * mm});
            skLineSegment(sketch, "E94.top", {"start": v(1373.82, 2088.84) * mm, "end": v(1141.34, 2088.84) * mm});
            skLineSegment(sketch, "E94.left", {"start": v(1373.82, 1866.9) * mm, "end": v(1373.82, 2088.84) * mm});
            skLineSegment(sketch, "E94.right", {"start": v(1141.34, 1866.9) * mm, "end": v(1141.34, 2088.84) * mm});
            skLineSegment(sketch, "E95.bottom", {"start": v(1618.82, 1866.9) * mm, "end": v(1373.82, 1866.9) * mm});
            skLineSegment(sketch, "E95.top", {"start": v(1618.82, 1977.87) * mm, "end": v(1373.82, 1977.87) * mm});
            skLineSegment(sketch, "E95.left", {"start": v(1618.82, 1866.9) * mm, "end": v(1618.82, 1977.87) * mm});
            skLineSegment(sketch, "E95.right", {"start": v(1373.82, 1866.9) * mm, "end": v(1373.82, 1977.87) * mm});
            skLineSegment(sketch, "E96.bottom", {"start": v(1618.82, 1922.38) * mm, "end": v(1653.28, 1922.38) * mm});
            skLineSegment(sketch, "E96.top", {"start": v(1618.82, 1866.9) * mm, "end": v(1653.28, 1866.9) * mm});
            skLineSegment(sketch, "E96.left", {"start": v(1618.82, 1922.38) * mm, "end": v(1618.82, 1866.9) * mm});
            skLineSegment(sketch, "E96.right", {"start": v(1653.28, 1922.38) * mm, "end": v(1653.28, 1866.9) * mm});
            skLineSegment(sketch, "E97.bottom", {"start": v(-700.07, 2000.78) * mm, "end": v(-606.18, 2000.78) * mm});
            skLineSegment(sketch, "E97.top", {"start": v(-700.07, 1942.41) * mm, "end": v(-606.18, 1942.41) * mm});
            skLineSegment(sketch, "E97.left", {"start": v(-700.07, 2000.78) * mm, "end": v(-700.07, 1942.41) * mm});
            skLineSegment(sketch, "E97.right", {"start": v(-606.18, 2000.78) * mm, "end": v(-606.18, 1942.41) * mm});
            skPoint(sketch, "E98.oppositeSnap0", {"position": v(1257.58, 1866.9) * mm});
            skLineSegment(sketch, "E98.bottom", {"start": v(916.98, 1923.57) * mm, "end": v(1257.58, 1923.57) * mm});
            skLineSegment(sketch, "E98.top", {"start": v(916.98, 1870.38) * mm, "end": v(1257.58, 1870.38) * mm});
            skLineSegment(sketch, "E98.left", {"start": v(916.98, 1923.57) * mm, "end": v(916.98, 1870.38) * mm});
            skLineSegment(sketch, "E98.right", {"start": v(1257.58, 1923.57) * mm, "end": v(1257.58, 1870.38) * mm});
            skSolve(sketch);
        }
        {
            var Q0;
            Q0=makeQuery(id+"F28.opExtrude","CAP_FACE",FACE,{"disambiguationData":[OSD([sQuery(id+"F27.wireOp",EDGE,"E66.bottom"),sQuery(id+"F27.wireOp",EDGE,"E66.top"),sQuery(id+"F27.wireOp",EDGE,"E66.left"),sQuery(id+"F27.wireOp",EDGE,"E66.right"),sQuery(id+"F27.wireOp",EDGE,"E67.bottom"),sQuery(id+"F27.wireOp",EDGE,"E67.top"),sQuery(id+"F27.wireOp",EDGE,"E67.right"),sQuery(id+"F27.wireOp",EDGE,"E68.top"),sQuery(id+"F27.wireOp",EDGE,"E68.left"),sQuery(id+"F27.wireOp",EDGE,"E68.right"),sQuery(id+"F27.wireOp",EDGE,"E69.top"),sQuery(id+"F27.wireOp",EDGE,"E69.left"),sQuery(id+"F27.wireOp",EDGE,"E69.right")])],"isStart":false});
            var sketch = newSketch(context, id + "F31", { "sketchPlane" : qUnion([Q0])});
            skLineSegment(sketch, "E99.0", {"start": v(-1191.52, 1377.95) * mm, "end": v(1653.28, 1377.95) * mm, "construction": true});
            skLineSegment(sketch, "E100.0", {"start": v(-1197.87, 1727.2) * mm, "end": v(681.73, 1727.2) * mm, "construction": true});
            skLineSegment(sketch, "E101.0", {"start": v(-1191.52, 1866.9) * mm, "end": v(1653.28, 1866.9) * mm, "construction": true});
            skLineSegment(sketch, "E102", {"start": v(-799.2, 2089.15) * mm, "end": v(1687.96, 2089.15) * mm, "construction": true});
            skLineSegment(sketch, "E103", {"start": v(-1191.52, 1377.95) * mm, "end": v(-1191.52, 2050.72) * mm});
            skLineSegment(sketch, "E104", {"start": v(-1191.52, 2050.72) * mm, "end": v(-996.5, 2050.72) * mm});
            skLineSegment(sketch, "E105", {"start": v(-996.5, 2050.72) * mm, "end": v(-996.5, 1897.6) * mm});
            skLineSegment(sketch, "E106", {"start": v(-996.5, 1897.6) * mm, "end": v(-929.13, 1897.6) * mm});
            skLineSegment(sketch, "E107", {"start": v(-929.13, 1897.6) * mm, "end": v(-929.13, 1983.35) * mm});
            skLineSegment(sketch, "E108", {"start": v(-929.13, 1983.35) * mm, "end": v(-794.4, 1983.35) * mm});
            skLineSegment(sketch, "E109", {"start": v(-794.4, 1983.35) * mm, "end": v(-794.4, 2089.15) * mm});
            skLineSegment(sketch, "E110", {"start": v(-794.4, 2089.15) * mm, "end": v(-181.81, 2089.15) * mm});
            skLineSegment(sketch, "E111", {"start": v(-181.81, 2089.15) * mm, "end": v(-181.81, 2016.97) * mm});
            skLineSegment(sketch, "E112", {"start": v(-181.81, 2016.97) * mm, "end": v(-18.5, 2016.97) * mm});
            skLineSegment(sketch, "E113", {"start": v(-18.5, 2016.97) * mm, "end": v(-18.5, 2069.09) * mm});
            skLineSegment(sketch, "E114", {"start": v(-18.5, 2069.09) * mm, "end": v(197.9, 2069.09) * mm});
            skLineSegment(sketch, "E115", {"start": v(197.9, 2069.09) * mm, "end": v(197.9, 1950.69) * mm});
            skLineSegment(sketch, "E116", {"start": v(197.9, 1950.69) * mm, "end": v(271.38, 1950.69) * mm});
            skLineSegment(sketch, "E117", {"start": v(271.38, 1950.69) * mm, "end": v(271.38, 2020.4) * mm});
            skLineSegment(sketch, "E118", {"start": v(271.38, 2020.4) * mm, "end": v(414.28, 2020.4) * mm});
            skLineSegment(sketch, "E119", {"start": v(414.28, 2020.4) * mm, "end": v(414.28, 1977.23) * mm});
            skLineSegment(sketch, "E120", {"start": v(414.28, 1977.23) * mm, "end": v(536.76, 1977.23) * mm});
            skLineSegment(sketch, "E121", {"start": v(536.76, 1977.23) * mm, "end": v(536.76, 2069.09) * mm});
            skLineSegment(sketch, "E122", {"start": v(536.76, 2069.09) * mm, "end": v(702.12, 2069.09) * mm});
            skLineSegment(sketch, "E123", {"start": v(702.12, 2069.09) * mm, "end": v(702.12, 1943.7) * mm});
            skLineSegment(sketch, "E124", {"start": v(702.12, 1943.7) * mm, "end": v(851.14, 1943.7) * mm});
            skLineSegment(sketch, "E125", {"start": v(851.14, 1943.7) * mm, "end": v(851.14, 2038.47) * mm});
            skLineSegment(sketch, "E126", {"start": v(851.14, 2038.47) * mm, "end": v(1094.07, 2038.47) * mm});
            skLineSegment(sketch, "E127", {"start": v(1094.07, 2038.47) * mm, "end": v(1094.07, 1983.35) * mm});
            skLineSegment(sketch, "E128", {"start": v(1094.07, 1983.35) * mm, "end": v(1094.07, 2089.15) * mm});
            skLineSegment(sketch, "E129", {"start": v(1094.07, 2089.15) * mm, "end": v(1369.66, 2089.15) * mm});
            skLineSegment(sketch, "E130", {"start": v(1369.66, 2089.15) * mm, "end": v(1467.65, 2089.15) * mm});
            skLineSegment(sketch, "E131", {"start": v(1467.65, 2089.15) * mm, "end": v(1467.65, 1944.56) * mm});
            skLineSegment(sketch, "E132", {"start": v(1467.65, 1944.56) * mm, "end": v(1576.53, 1944.56) * mm});
            skLineSegment(sketch, "E133", {"start": v(1576.53, 1944.56) * mm, "end": v(1576.53, 1927.44) * mm});
            skLineSegment(sketch, "E134", {"start": v(1576.53, 1927.44) * mm, "end": v(1653.28, 1927.44) * mm});
            skLineSegment(sketch, "E135", {"start": v(1653.28, 1927.44) * mm, "end": v(1653.28, 1377.95) * mm});
            skLineSegment(sketch, "E136.bottom", {"start": v(-737.08, 2007.85) * mm, "end": v(-622.76, 2007.85) * mm});
            skLineSegment(sketch, "E136.top", {"start": v(-737.08, 1956.81) * mm, "end": v(-622.76, 1956.81) * mm});
            skLineSegment(sketch, "E136.left", {"start": v(-737.08, 2007.85) * mm, "end": v(-737.08, 1956.81) * mm});
            skLineSegment(sketch, "E136.right", {"start": v(-622.76, 2007.85) * mm, "end": v(-622.76, 1956.81) * mm});
            skLineSegment(sketch, "E137.bottom", {"start": v(953.21, 1944.56) * mm, "end": v(1304.34, 1944.56) * mm});
            skLineSegment(sketch, "E137.top", {"start": v(953.21, 1903.73) * mm, "end": v(1304.34, 1903.73) * mm});
            skLineSegment(sketch, "E137.left", {"start": v(953.21, 1944.56) * mm, "end": v(953.21, 1903.73) * mm});
            skLineSegment(sketch, "E137.right", {"start": v(1304.34, 1944.56) * mm, "end": v(1304.34, 1903.73) * mm});
            skLineSegment(sketch, "E138.bottom", {"start": v(20.29, 2036.43) * mm, "end": v(57.03, 2036.43) * mm});
            skLineSegment(sketch, "E138.top", {"start": v(20.29, 2005.8) * mm, "end": v(57.03, 2005.8) * mm});
            skLineSegment(sketch, "E138.left", {"start": v(20.29, 2036.43) * mm, "end": v(20.29, 2005.8) * mm});
            skLineSegment(sketch, "E138.right", {"start": v(57.03, 2036.43) * mm, "end": v(57.03, 2005.8) * mm});
            skLineSegment(sketch, "E139.bottom", {"start": v(118.27, 2038.47) * mm, "end": v(155.02, 2038.47) * mm});
            skLineSegment(sketch, "E139.top", {"start": v(118.27, 2001.72) * mm, "end": v(155.02, 2001.72) * mm});
            skLineSegment(sketch, "E139.left", {"start": v(118.27, 2038.47) * mm, "end": v(118.27, 2001.72) * mm});
            skLineSegment(sketch, "E139.right", {"start": v(155.02, 2038.47) * mm, "end": v(155.02, 2001.72) * mm});
            skLineSegment(sketch, "E140", {"start": v(-1191.52, 1377.95) * mm, "end": v(1653.28, 1377.95) * mm});
            skSolve(sketch);
        }
        {
            var Q0;
            Q0=qSketchRegion(id+"F31",true);
            extrude(context, id + "F32", {"entities" : qUnion([Q0]), "depth" : 6.35 * mm});
        }
        {
            var Q0;
            Q0=makeQuery(id+"F20.opExtrude","CAP_FACE",FACE,{"disambiguationData":[OSD([sQuery(id+"F19.wireOp",EDGE,"E31.0.1.0"),sQuery(id+"F19.wireOp",EDGE,"E31.0.1.1"),sQuery(id+"F19.wireOp",EDGE,"E31.0.1.2"),sQuery(id+"F19.wireOp",EDGE,"E31.0.1.3")])],"isStart":false});
            var sketch = newSketch(context, id + "F33", { "sketchPlane" : qUnion([Q0])});
            skPoint(sketch, "E141.0", {"position": v(1191.52, 512.27) * mm});
            skLineSegment(sketch, "E142.bottom", {"start": v(1191.52, 512.27) * mm, "end": v(1051.82, 512.27) * mm});
            skLineSegment(sketch, "E142.top", {"start": v(1191.52, 474.17) * mm, "end": v(1051.82, 474.17) * mm});
            skLineSegment(sketch, "E142.left", {"start": v(1191.52, 512.27) * mm, "end": v(1191.52, 474.17) * mm});
            skLineSegment(sketch, "E142.right", {"start": v(1051.82, 512.27) * mm, "end": v(1051.82, 474.17) * mm});
            skPoint(sketch, "E143.0", {"position": v(-2212.08, 512.27) * mm});
            skLineSegment(sketch, "E144.bottom", {"start": v(-2212.08, 512.27) * mm, "end": v(-2072.38, 512.27) * mm});
            skLineSegment(sketch, "E144.top", {"start": v(-2212.08, 474.17) * mm, "end": v(-2072.38, 474.17) * mm});
            skLineSegment(sketch, "E144.left", {"start": v(-2212.08, 512.27) * mm, "end": v(-2212.08, 474.17) * mm});
            skLineSegment(sketch, "E144.right", {"start": v(-2072.38, 512.27) * mm, "end": v(-2072.38, 474.17) * mm});
            skPoint(sketch, "E145.0", {"position": v(-2212.08, -910.13) * mm});
            skLineSegment(sketch, "E146.bottom", {"start": v(-2212.08, -910.13) * mm, "end": v(-2072.38, -910.13) * mm});
            skLineSegment(sketch, "E146.top", {"start": v(-2212.08, -872.03) * mm, "end": v(-2072.38, -872.03) * mm});
            skLineSegment(sketch, "E146.left", {"start": v(-2212.08, -910.13) * mm, "end": v(-2212.08, -872.03) * mm});
            skLineSegment(sketch, "E146.right", {"start": v(-2072.38, -910.13) * mm, "end": v(-2072.38, -872.03) * mm});
            skPoint(sketch, "E147.0", {"position": v(1191.52, -910.13) * mm});
            skLineSegment(sketch, "E148.bottom", {"start": v(1191.52, -910.13) * mm, "end": v(1051.82, -910.13) * mm});
            skLineSegment(sketch, "E148.top", {"start": v(1191.52, -872.03) * mm, "end": v(1051.82, -872.03) * mm});
            skLineSegment(sketch, "E148.left", {"start": v(1191.52, -910.13) * mm, "end": v(1191.52, -872.03) * mm});
            skLineSegment(sketch, "E148.right", {"start": v(1051.82, -910.13) * mm, "end": v(1051.82, -872.03) * mm});
            skSolve(sketch);
        }
        {
            var Q0;
            Q0=qSketchRegion(id+"F33",true);
            var Q1;
            Q1=makeQuery(id+"F26.opPattern","COPY",FACE,{"derivedFrom":makeQuery(id+"F22.opExtrude","SWEPT_FACE",FACE,{"disambiguationData":[OSD([sQuery(id+"F21.wireOp",EDGE,"E55")])]}),"instanceName":"1"});
            extrude(context, id + "F34", {"entities" : qUnion([Q0]), "endBound" : BoundingType.UP_TO_SURFACE, "endBoundEntityFace" : qUnion([Q1]), "depth" : 25.4 * mm});
        }
        {
            var Q0;
            Q0=makeQuery(id+"F18.opExtrude","CAP_FACE",FACE,{"disambiguationData":[OSD([sQuery(id+"F17.wireOp",EDGE,"E18.bottom"),sQuery(id+"F17.wireOp",EDGE,"E18.top"),sQuery(id+"F17.wireOp",EDGE,"E18.left"),sQuery(id+"F17.wireOp",EDGE,"E18.right")])],"isStart":true});
            var sketch = newSketch(context, id + "F35", { "sketchPlane" : qUnion([Q0])});
            skPoint(sketch, "E149", {"position": v(-2212.08, -474.17) * mm});
            skPoint(sketch, "E150", {"position": v(-2212.08, 872.03) * mm});
            skPoint(sketch, "E151.0", {"position": v(1191.52, 872.03) * mm});
            skPoint(sketch, "E152.0", {"position": v(1191.52, -474.17) * mm});
            skLineSegment(sketch, "E153.bottom", {"start": v(-2212.08, 872.03) * mm, "end": v(-2072.38, 872.03) * mm});
            skLineSegment(sketch, "E153.top", {"start": v(-2212.08, 833.93) * mm, "end": v(-2072.38, 833.93) * mm});
            skLineSegment(sketch, "E153.left", {"start": v(-2212.08, 872.03) * mm, "end": v(-2212.08, 833.93) * mm});
            skLineSegment(sketch, "E153.right", {"start": v(-2072.38, 872.03) * mm, "end": v(-2072.38, 833.93) * mm});
            skLineSegment(sketch, "E154.bottom", {"start": v(1191.52, 872.03) * mm, "end": v(1051.82, 872.03) * mm});
            skLineSegment(sketch, "E154.top", {"start": v(1191.52, 833.93) * mm, "end": v(1051.82, 833.93) * mm});
            skLineSegment(sketch, "E154.left", {"start": v(1191.52, 872.03) * mm, "end": v(1191.52, 833.93) * mm});
            skLineSegment(sketch, "E154.right", {"start": v(1051.82, 872.03) * mm, "end": v(1051.82, 833.93) * mm});
            skLineSegment(sketch, "E155.bottom", {"start": v(1191.52, -474.17) * mm, "end": v(1051.82, -474.17) * mm});
            skLineSegment(sketch, "E155.top", {"start": v(1191.52, -436.07) * mm, "end": v(1051.82, -436.07) * mm});
            skLineSegment(sketch, "E155.left", {"start": v(1191.52, -474.17) * mm, "end": v(1191.52, -436.07) * mm});
            skLineSegment(sketch, "E155.right", {"start": v(1051.82, -474.17) * mm, "end": v(1051.82, -436.07) * mm});
            skLineSegment(sketch, "E156.bottom", {"start": v(-2212.08, -474.17) * mm, "end": v(-2072.38, -474.17) * mm});
            skLineSegment(sketch, "E156.top", {"start": v(-2212.08, -436.07) * mm, "end": v(-2072.38, -436.07) * mm});
            skLineSegment(sketch, "E156.left", {"start": v(-2212.08, -474.17) * mm, "end": v(-2212.08, -436.07) * mm});
            skLineSegment(sketch, "E156.right", {"start": v(-2072.38, -474.17) * mm, "end": v(-2072.38, -436.07) * mm});
            skSolve(sketch);
        }
        {
            var Q0;
            Q0=qSketchRegion(id+"F35",true);
            var Q1;
            {Q1=qUnion([makeQuery(id+"F34.opExtrude","CAP_FACE",FACE,{"disambiguationData":[OSD([sQuery(id+"F33.wireOp",EDGE,"E142.bottom"),sQuery(id+"F33.wireOp",EDGE,"E142.top"),sQuery(id+"F33.wireOp",EDGE,"E142.left"),sQuery(id+"F33.wireOp",EDGE,"E142.right")])],"isStart":false}),makeQuery(id+"F34.opExtrude","CAP_FACE",FACE,{"disambiguationData":[OSD([sQuery(id+"F33.wireOp",EDGE,"E144.bottom"),sQuery(id+"F33.wireOp",EDGE,"E144.top"),sQuery(id+"F33.wireOp",EDGE,"E144.left"),sQuery(id+"F33.wireOp",EDGE,"E144.right")])],"isStart":false}),makeQuery(id+"F34.opExtrude","CAP_FACE",FACE,{"disambiguationData":[OSD([sQuery(id+"F33.wireOp",EDGE,"E146.bottom"),sQuery(id+"F33.wireOp",EDGE,"E146.top"),sQuery(id+"F33.wireOp",EDGE,"E146.left"),sQuery(id+"F33.wireOp",EDGE,"E146.right")])],"isStart":false}),makeQuery(id+"F34.opExtrude","CAP_FACE",FACE,{"disambiguationData":[OSD([sQuery(id+"F33.wireOp",EDGE,"E148.bottom"),sQuery(id+"F33.wireOp",EDGE,"E148.top"),sQuery(id+"F33.wireOp",EDGE,"E148.left"),sQuery(id+"F33.wireOp",EDGE,"E148.right")])],"isStart":false})]);}
            extrude(context, id + "F36", {"entities" : qUnion([Q0]), "endBound" : BoundingType.UP_TO_SURFACE, "oppositeDirection" : true, "endBoundEntityFace" : qUnion([Q1]), "depth" : 25.4 * mm});
        }
        {
            var Q0;
            Q0=makeQuery(id+"F18.opExtrude","SWEPT_BODY",BODY,{"disambiguationData":[OSD([sQuery(id+"F17.wireOp",EDGE,"E18.bottom"),sQuery(id+"F17.wireOp",EDGE,"E18.top"),sQuery(id+"F17.wireOp",EDGE,"E18.left"),sQuery(id+"F17.wireOp",EDGE,"E18.right")])]});
            var Q1;
            Q1=makeQuery(id+"F18.opExtrude","SWEPT_BODY",BODY,{"disambiguationData":[OSD([sQuery(id+"F17.wireOp",EDGE,"E19.bottom"),sQuery(id+"F17.wireOp",EDGE,"E19.top"),sQuery(id+"F17.wireOp",EDGE,"E19.left"),sQuery(id+"F17.wireOp",EDGE,"E19.right")])]});
            var Q2;
            Q2=makeQuery(id+"F36.opExtrude","SWEPT_BODY",BODY,{"disambiguationData":[OSD([sQuery(id+"F35.wireOp",EDGE,"E156.bottom"),sQuery(id+"F35.wireOp",EDGE,"E156.top"),sQuery(id+"F35.wireOp",EDGE,"E156.left"),sQuery(id+"F35.wireOp",EDGE,"E156.right")])]});
            var Q3;
            Q3=makeQuery(id+"F36.opExtrude","SWEPT_BODY",BODY,{"disambiguationData":[OSD([sQuery(id+"F35.wireOp",EDGE,"E153.bottom"),sQuery(id+"F35.wireOp",EDGE,"E153.top"),sQuery(id+"F35.wireOp",EDGE,"E153.left"),sQuery(id+"F35.wireOp",EDGE,"E153.right")])]});
            var Q4;
            Q4=makeQuery(id+"F36.opExtrude","SWEPT_BODY",BODY,{"disambiguationData":[OSD([sQuery(id+"F35.wireOp",EDGE,"E154.bottom"),sQuery(id+"F35.wireOp",EDGE,"E154.top"),sQuery(id+"F35.wireOp",EDGE,"E154.left"),sQuery(id+"F35.wireOp",EDGE,"E154.right")])]});
            var Q5;
            Q5=makeQuery(id+"F36.opExtrude","SWEPT_BODY",BODY,{"disambiguationData":[OSD([sQuery(id+"F35.wireOp",EDGE,"E155.bottom"),sQuery(id+"F35.wireOp",EDGE,"E155.top"),sQuery(id+"F35.wireOp",EDGE,"E155.left"),sQuery(id+"F35.wireOp",EDGE,"E155.right")])]});
            booleanBodies(context, id + "F37", {"operationType" : BooleanOperationType.SUBTRACTION, "tools" : qUnion([Q0, Q1]), "targets" : qUnion([Q2, Q3, Q4, Q5]), "keepTools" : true});
        }
        {
            var Q0;
            Q0=makeQuery(id+"F28.opExtrude","CAP_FACE",FACE,{"disambiguationData":[OSD([sQuery(id+"F27.wireOp",EDGE,"E66.bottom"),sQuery(id+"F27.wireOp",EDGE,"E66.top"),sQuery(id+"F27.wireOp",EDGE,"E66.left"),sQuery(id+"F27.wireOp",EDGE,"E66.right"),sQuery(id+"F27.wireOp",EDGE,"E67.bottom"),sQuery(id+"F27.wireOp",EDGE,"E67.top"),sQuery(id+"F27.wireOp",EDGE,"E67.right"),sQuery(id+"F27.wireOp",EDGE,"E68.top"),sQuery(id+"F27.wireOp",EDGE,"E68.left"),sQuery(id+"F27.wireOp",EDGE,"E68.right"),sQuery(id+"F27.wireOp",EDGE,"E69.top"),sQuery(id+"F27.wireOp",EDGE,"E69.left"),sQuery(id+"F27.wireOp",EDGE,"E69.right")])],"isStart":false});
            var sketch = newSketch(context, id + "F38", { "sketchPlane" : qUnion([Q0])});
            skLineSegment(sketch, "E157.bottom", {"start": v(-1191.52, 1377.95) * mm, "end": v(1654.4, 1377.95) * mm});
            skLineSegment(sketch, "E157.top", {"start": v(-1191.52, 2000.25) * mm, "end": v(1653.28, 2000.25) * mm, "construction": true});
            skLineSegment(sketch, "E157.left", {"start": v(-1191.52, 1377.95) * mm, "end": v(-1191.52, 1866.9) * mm});
            skArc(sketch, "E158", {"start": v(-716.26, 1868.71) * mm, "mid": v(-954.4, 2000.25) * mm, "end": v(-1191.52, 1866.9) * mm});
            skArc(sketch, "E159.1.0.0", {"start": v(-242.13, 1868.71) * mm, "mid": v(-479.2, 2000.25) * mm, "end": v(-716.26, 1868.71) * mm});
            skArc(sketch, "E159.2.0.0", {"start": v(232, 1868.71) * mm, "mid": v(-5.06, 2000.25) * mm, "end": v(-242.13, 1868.71) * mm});
            skArc(sketch, "E159.3.0.0", {"start": v(706.14, 1868.71) * mm, "mid": v(469.07, 2000.25) * mm, "end": v(232, 1868.71) * mm});
            skArc(sketch, "E159.4.0.0", {"start": v(1180.27, 1868.71) * mm, "mid": v(943.2, 2000.25) * mm, "end": v(706.14, 1868.71) * mm});
            skArc(sketch, "E159.5.0.0", {"start": v(1654.4, 1868.71) * mm, "mid": v(1417.34, 2000.25) * mm, "end": v(1180.27, 1868.71) * mm});
            skLineSegment(sketch, "E159.direction1", {"start": v(-988.32, 1885.95) * mm, "end": v(-514.18, 1885.95) * mm, "construction": true});
            skPoint(sketch, "E160.0", {"position": v(-1191.52, 1866.9) * mm});
            skLineSegment(sketch, "E161", {"start": v(-1191.52, 1866.9) * mm, "end": v(-1191.52, 1377.95) * mm});
            skLineSegment(sketch, "E162", {"start": v(1654.4, 1377.95) * mm, "end": v(1654.4, 1868.71) * mm});
            skLineSegment(sketch, "E163", {"start": v(1654.4, 1377.95) * mm, "end": v(-1191.52, 1377.95) * mm});
            skLineSegment(sketch, "E164.bottom", {"start": v(-1191.52, 1866.9) * mm, "end": v(1653.28, 1866.9) * mm, "construction": true});
            skLineSegment(sketch, "E165", {"start": v(1878.23, 1868.71) * mm, "end": v(-1806.86, 1868.71) * mm, "construction": true});
            skSolve(sketch);
        }
        {
            var Q0;
            Q0 = qSketchRegion(id + "F38", true);
            extrude(context, id + "F39", {"entities" : qUnion([Q0]), "depth" : 6.35 * mm});
        }
        {
            var Q0;
            Q0=makeQuery(id+"F39.opExtrude","SWEPT_EDGE",EDGE,{"disambiguationData":[OSD([sQuery(id+"F38.wireOp",EDGE,"E158"),sQuery(id+"F38.wireOp",EDGE,"E164.bottom"),sQuery(id+"F38.wireOp",EDGE,"E161")])]});
            var Q1;
            Q1=makeQuery(id+"F39.opExtrude","SWEPT_EDGE",EDGE,{"disambiguationData":[OSD([sQuery(id+"F38.wireOp",EDGE,"E158"),sQuery(id+"F38.wireOp",EDGE,"E159.1.0.0")])]});
            var Q2;
            Q2=makeQuery(id+"F39.opExtrude","SWEPT_EDGE",EDGE,{"disambiguationData":[OSD([sQuery(id+"F38.wireOp",EDGE,"E159.1.0.0"),sQuery(id+"F38.wireOp",EDGE,"E159.2.0.0")])]});
            var Q3;
            Q3=makeQuery(id+"F39.opExtrude","SWEPT_EDGE",EDGE,{"disambiguationData":[OSD([sQuery(id+"F38.wireOp",EDGE,"E159.2.0.0"),sQuery(id+"F38.wireOp",EDGE,"E159.3.0.0")])]});
            var Q4;
            Q4=makeQuery(id+"F39.opExtrude","SWEPT_EDGE",EDGE,{"disambiguationData":[OSD([sQuery(id+"F38.wireOp",EDGE,"E159.3.0.0"),sQuery(id+"F38.wireOp",EDGE,"E159.4.0.0")])]});
            var Q5;
            Q5=makeQuery(id+"F39.opExtrude","SWEPT_EDGE",EDGE,{"disambiguationData":[OSD([sQuery(id+"F38.wireOp",EDGE,"E159.4.0.0"),sQuery(id+"F38.wireOp",EDGE,"E159.5.0.0")])]});
            var Q6;
            Q6=makeQuery(id+"F39.opExtrude","SWEPT_EDGE",EDGE,{"disambiguationData":[OSD([sQuery(id+"F38.wireOp",EDGE,"E159.5.0.0"),sQuery(id+"F38.wireOp",EDGE,"E162")])]});
            var Q7;
            Q7=makeQuery(id+"F39.opExtrude","SWEPT_EDGE",EDGE,{"disambiguationData":[OSD([sQuery(id+"F38.wireOp",EDGE,"E157.bottom"),sQuery(id+"F38.wireOp",EDGE,"E164.right")])]});
            fillet(context, id + "F40", {"entities" : qUnion([Q0, Q1, Q2, Q3, Q4, Q5, Q6, Q7]), "radius" : 3.17 * mm, "tangentPropagation" : true, "allowEdgeOverflow" : false});
        }
        {
            var Q0;
            Q0=makeQuery(id+"F9.opExtrude","CAP_FACE",FACE,{"disambiguationData":[OSD([sQuery(id+"F8.wireOp",EDGE,"E12.bottom"),sQuery(id+"F8.wireOp",EDGE,"E12.top"),sQuery(id+"F8.wireOp",EDGE,"E12.left"),sQuery(id+"F8.wireOp",EDGE,"E12.right")])],"isStart":true});
            var sketch = newSketch(context, id + "F41", { "sketchPlane" : qUnion([Q0])});
            skCircle(sketch, "E166", {"center": v(500.74, 1493.88) * mm, "radius": 237.33 * mm});
            skSolve(sketch);
        }
        {
            var Q0;
            Q0 = qSketchRegion(id + "F41", true);
            extrude(context, id + "F42", {"entities" : qUnion([Q0]), "operationType" : NewBodyOperationType.ADD, "depth" : 1828.8 * mm});
        }
        {
            var Q0;
            Q0=makeQuery(id+"F9.opExtrude","CAP_FACE",FACE,{"disambiguationData":[OSD([sQuery(id+"F8.wireOp",EDGE,"E12.bottom"),sQuery(id+"F8.wireOp",EDGE,"E12.top"),sQuery(id+"F8.wireOp",EDGE,"E12.left"),sQuery(id+"F8.wireOp",EDGE,"E12.right")])],"isStart":true});
            var sketch = newSketch(context, id + "F43", { "sketchPlane" : qUnion([Q0])});
            skCircle(sketch, "E167", {"center": v(0, 1493.09) * mm, "radius": 169.53 * mm});
            skSolve(sketch);
        }
        {
            var Q0;
            Q0 = qSketchRegion(id + "F43", true);
            extrude(context, id + "F44", {"entities" : qUnion([Q0]), "operationType" : NewBodyOperationType.ADD, "depth" : 1600.2 * mm});
        }
        {
            var Q0;
            Q0=makeQuery(id+"F39.opExtrude","CAP_FACE",FACE,{"disambiguationData":[OSD([sQuery(id+"F38.wireOp",EDGE,"E158"),sQuery(id+"F38.wireOp",EDGE,"E159.1.0.0"),sQuery(id+"F38.wireOp",EDGE,"E159.2.0.0"),sQuery(id+"F38.wireOp",EDGE,"E159.3.0.0"),sQuery(id+"F38.wireOp",EDGE,"E159.4.0.0"),sQuery(id+"F38.wireOp",EDGE,"E159.5.0.0"),sQuery(id+"F38.wireOp",EDGE,"E162"),sQuery(id+"F38.wireOp",EDGE,"E157.bottom"),sQuery(id+"F38.wireOp",EDGE,"E161")])],"isStart":false});
            var sketch = newSketch(context, id + "F45", { "sketchPlane" : qUnion([Q0])});
            skLineSegment(sketch, "E168.right", {"start": v(232, 1377.95) * mm, "end": v(232, 1877.8) * mm});
            skPoint(sketch, "E169", {"position": v(232, 1877.8) * mm});
            skArc(sketch, "E170.0", {"start": v(-718.92, 1872.9) * mm, "mid": v(-956.42, 2000.23) * mm, "end": v(-1191.04, 1867.67) * mm});
            skArc(sketch, "E171.0", {"start": v(-244.8, 1872.9) * mm, "mid": v(-479.2, 2000.25) * mm, "end": v(-713.6, 1872.9) * mm});
            skArc(sketch, "E172.0", {"start": v(229.34, 1872.9) * mm, "mid": v(-5.06, 2000.25) * mm, "end": v(-239.46, 1872.9) * mm});
            skArc(sketch, "E173.0", {"start": v(-239.46, 1872.9) * mm, "mid": v(-242.13, 1871.45) * mm, "end": v(-244.8, 1872.9) * mm});
            skArc(sketch, "E174.0", {"start": v(-713.6, 1872.9) * mm, "mid": v(-716.26, 1871.45) * mm, "end": v(-718.92, 1872.9) * mm});
            skArc(sketch, "E175.0", {"start": v(-1191.04, 1867.67) * mm, "mid": v(-1191.4, 1866.87) * mm, "end": v(-1191.52, 1866) * mm});
            skLineSegment(sketch, "E176.0", {"start": v(-1191.52, 1381.13) * mm, "end": v(-1191.52, 1866) * mm});
            skArc(sketch, "E177.0", {"start": v(-1191.52, 1381.13) * mm, "mid": v(-1190.59, 1378.88) * mm, "end": v(-1188.34, 1377.95) * mm});
            skLineSegment(sketch, "E178.0", {"start": v(-1188.34, 1377.95) * mm, "end": v(1651.23, 1377.95) * mm});
            skArc(sketch, "E179.0", {"start": v(232, 1877.8) * mm, "mid": v(234.8, 1873.11) * mm, "end": v(229.34, 1872.9) * mm});
            skPoint(sketch, "E180.orphan", {"position": v(234.67, 1872.9) * mm});
            skPoint(sketch, "E168.top.end.orphan", {"position": v(234.67, 2020.63) * mm});
            skSolve(sketch);
        }
        {
            var Q0;
            Q0 = qSketchRegion(id + "F45", true);
            extrude(context, id + "F46", {"entities" : qUnion([Q0]), "oppositeDirection" : true, "depth" : 6.35 * mm});
        }
        {
            var Q0;
            Q0=makeQuery(id+"F46.opExtrude","SWEPT_BODY",BODY,{"disambiguationData":[OSD([sQuery(id+"F45.wireOp",EDGE,"E168.right"),sQuery(id+"F45.wireOp",EDGE,"E170.0"),sQuery(id+"F45.wireOp",EDGE,"E171.0"),sQuery(id+"F45.wireOp",EDGE,"E172.0"),sQuery(id+"F45.wireOp",EDGE,"E173.0"),sQuery(id+"F45.wireOp",EDGE,"E174.0"),sQuery(id+"F45.wireOp",EDGE,"E175.0"),sQuery(id+"F45.wireOp",EDGE,"E176.0"),sQuery(id+"F45.wireOp",EDGE,"E177.0"),sQuery(id+"F45.wireOp",EDGE,"E178.0"),sQuery(id+"F45.wireOp",EDGE,"E179.0")])]});
            var Q1;
            Q1=makeQuery(id+"F39.opExtrude","SWEPT_BODY",BODY,{"disambiguationData":[OSD([sQuery(id+"F38.wireOp",EDGE,"E158"),sQuery(id+"F38.wireOp",EDGE,"E159.1.0.0"),sQuery(id+"F38.wireOp",EDGE,"E159.2.0.0"),sQuery(id+"F38.wireOp",EDGE,"E159.3.0.0"),sQuery(id+"F38.wireOp",EDGE,"E159.4.0.0"),sQuery(id+"F38.wireOp",EDGE,"E159.5.0.0"),sQuery(id+"F38.wireOp",EDGE,"E162"),sQuery(id+"F38.wireOp",EDGE,"E157.bottom"),sQuery(id+"F38.wireOp",EDGE,"E161")])]});
            booleanBodies(context, id + "F47", {"operationType" : BooleanOperationType.SUBTRACTION, "tools" : qUnion([Q0]), "targets" : qUnion([Q1]), "keepTools" : true});
        }
        {
            var Q0;
            Q0=makeQuery(id+"F18.opExtrude","SWEPT_FACE",FACE,{"disambiguationData":[OSD([sQuery(id+"F17.wireOp",EDGE,"E19.left")])]});
            var sketch = newSketch(context, id + "F48", { "sketchPlane" : qUnion([Q0])});
            skLineSegment(sketch, "E181", {"start": v(-53.8, 1377.95) * mm, "end": v(-436.07, 995.67) * mm});
            skLineSegment(sketch, "E182", {"start": v(-436.07, 995.67) * mm, "end": v(-436.07, 869.95) * mm});
            skLineSegment(sketch, "E183", {"start": v(-436.07, 869.95) * mm, "end": v(71.93, 1377.95) * mm});
            skLineSegment(sketch, "E184", {"start": v(71.93, 1377.95) * mm, "end": v(-53.8, 1377.95) * mm});
            skLineSegment(sketch, "E185", {"start": v(376.73, 1377.95) * mm, "end": v(502.45, 1377.95) * mm});
            skLineSegment(sketch, "E186", {"start": v(502.45, 1377.95) * mm, "end": v(833.93, 1046.47) * mm});
            skLineSegment(sketch, "E187", {"start": v(833.93, 1046.47) * mm, "end": v(833.93, 920.75) * mm});
            skLineSegment(sketch, "E188", {"start": v(833.93, 920.75) * mm, "end": v(376.73, 1377.95) * mm});
            skLineSegment(sketch, "E189.0", {"start": v(-436.07, 0) * mm, "end": v(-436.07, 1377.95) * mm, "construction": true});
            skLineSegment(sketch, "E190.0", {"start": v(833.93, 0) * mm, "end": v(833.93, 1377.95) * mm, "construction": true});
            skSolve(sketch);
        }
        {
            var Q0;
            Q0 = qSketchRegion(id + "F48", true);
            extrude(context, id + "F49", {"entities" : qUnion([Q0]), "oppositeDirection" : true, "depth" : 38.1 * mm});
        }
    });
